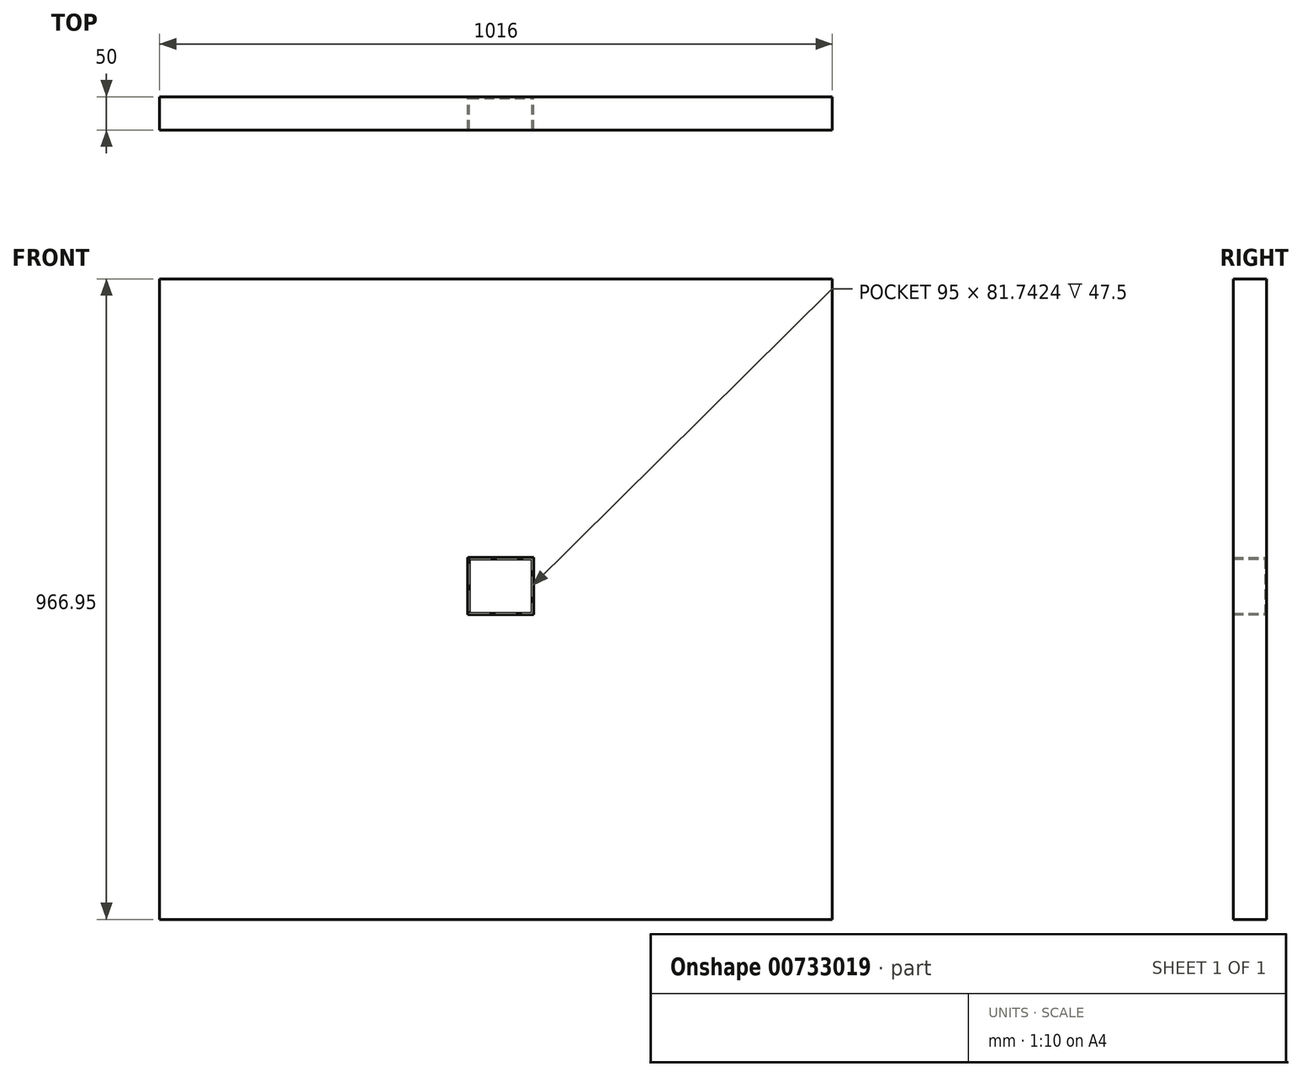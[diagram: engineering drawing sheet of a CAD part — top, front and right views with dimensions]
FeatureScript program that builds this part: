
annotation { "Feature Type Name" : "Feature", "Feature Type Description" : "" }
export const myFeature = defineFeature(function(context is Context, id is Id, definition is map)
    precondition{}
    {
        {
            var Q0;
            Q0=qCreatedBy(makeId("Front.planeOp"),FACE);
            var sketch = newSketch(context, id + "F0", { "sketchPlane" : qUnion([Q0])});
            skLineSegment(sketch, "E0.bottom", {"start": v(-42.9, 38.58) * mm, "end": v(57.1, 38.58) * mm});
            skLineSegment(sketch, "E0.top", {"start": v(-42.9, -48.16) * mm, "end": v(57.1, -48.16) * mm});
            skLineSegment(sketch, "E0.left", {"start": v(-42.9, 38.58) * mm, "end": v(-42.9, -48.16) * mm});
            skLineSegment(sketch, "E0.right", {"start": v(57.1, 38.58) * mm, "end": v(57.1, -48.16) * mm});
            skSolve(sketch);
        }
        {
            var Q0;
            Q0=makeQuery(id+"F0.imprint","IMPRINT",FACE,{"disambiguationData":[TD([[makeQuery(id+"F0.imprint","IMPRINT",EDGE,{"derivedFrom":sQuery(id+"F0.wireOp",EDGE,"E0.bottom")}),-1.0]])]});
            var sketch = newSketch(context, id + "F1", { "sketchPlane" : qUnion([Q0])});
            skLineSegment(sketch, "E1.bottom", {"start": v(-508, 458.95) * mm, "end": v(508, 458.95) * mm});
            skLineSegment(sketch, "E1.top", {"start": v(-508, -508) * mm, "end": v(508, -508) * mm});
            skLineSegment(sketch, "E1.left", {"start": v(-508, 458.95) * mm, "end": v(-508, -508) * mm});
            skLineSegment(sketch, "E1.right", {"start": v(508, 458.95) * mm, "end": v(508, -508) * mm});
            skSolve(sketch);
        }
        {
            var Q0;
            Q0 = qSketchRegion(id + "F0", true);
            var Q1;
            Q1 = qSketchRegion(id + "FY5KoWHMoJbLCTr_0", true);
            var Q2;
            Q2 = qSketchRegion(id + "F1", true);
            extrude(context, id + "F2", {"entities" : qUnion([Q0, Q1, Q2]), "depth" : 50 * mm, "offsetDistance" : 25 * mm});
        }
        {
            var Q0;
            Q0=makeQuery(id+"F2.opExtrude","CAP_FACE",FACE,{"disambiguationData":[OSD([sQuery(id+"F0.wireOp",EDGE,"E0.bottom"),sQuery(id+"F0.wireOp",EDGE,"E0.top"),sQuery(id+"F0.wireOp",EDGE,"E0.left"),sQuery(id+"F0.wireOp",EDGE,"E0.right")])],"isStart":false});
            shell(context, id + "F3", {"entities" : qUnion([Q0]), "thickness" : 2.5 * mm});
        }
    });
